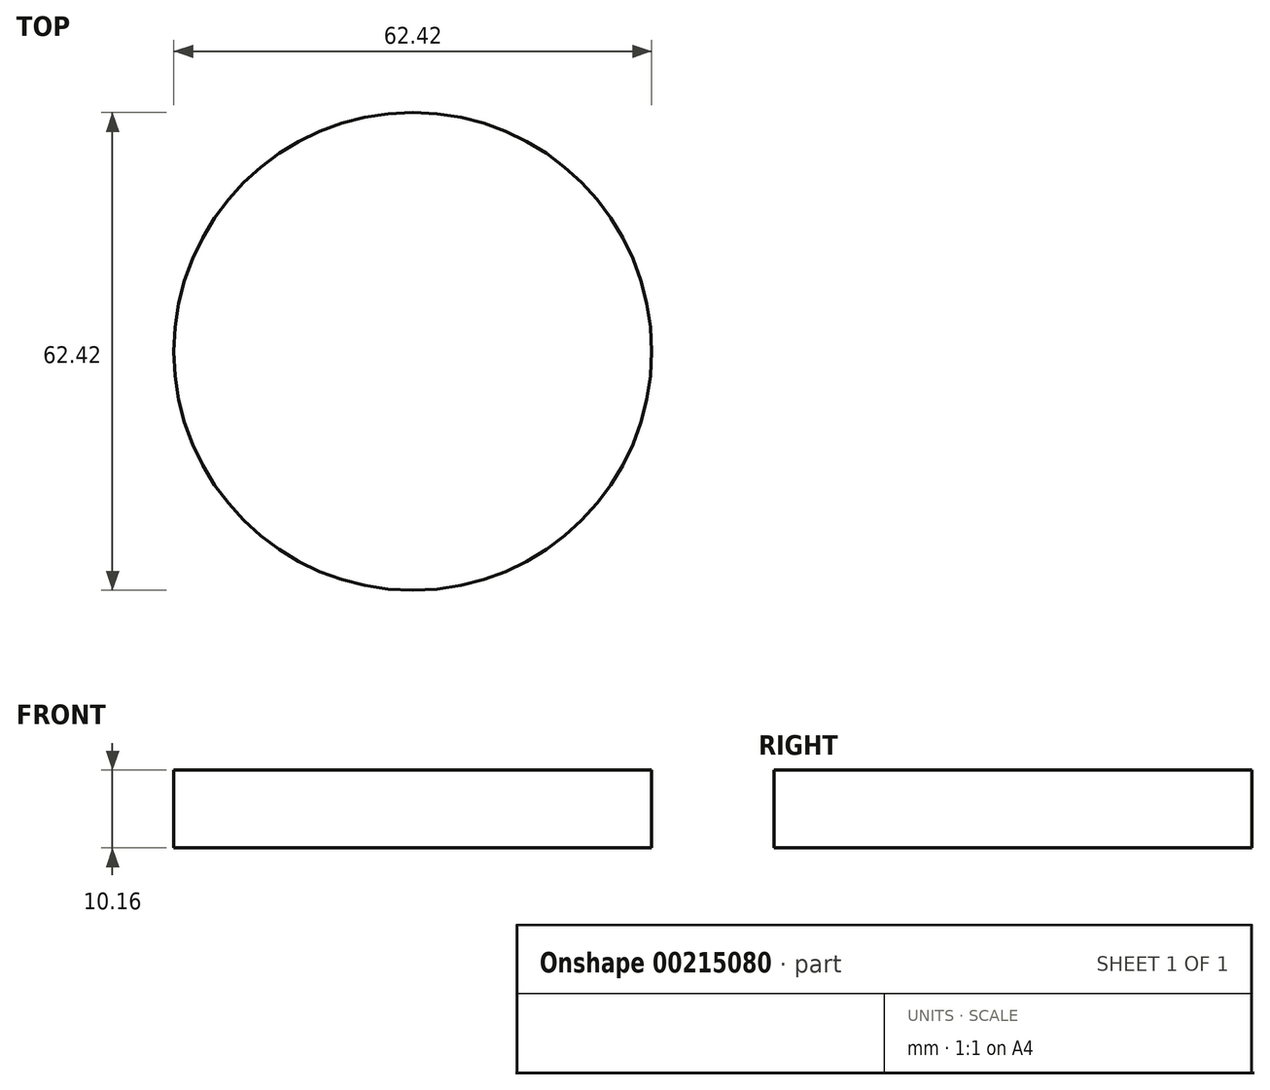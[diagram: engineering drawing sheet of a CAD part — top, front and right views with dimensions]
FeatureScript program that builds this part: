
annotation { "Feature Type Name" : "Feature", "Feature Type Description" : "" }
export const myFeature = defineFeature(function(context is Context, id is Id, definition is map)
    precondition{}
    {
        {
            var Q0;
            Q0=qCreatedBy(makeId("Top.planeOp"),FACE);
            var sketch = newSketch(context, id + "F0", { "sketchPlane" : qUnion([Q0])});
            skCircle(sketch, "E0", {"center": v(0, 0) * mm, "radius": 31.2 * mm});
            skSolve(sketch);
        }
        {
            var Q0;
            Q0=makeQuery(id+"F0.imprint","IMPRINT",FACE,{"disambiguationData":[TD([[makeQuery(id+"F0.imprint","IMPRINT",EDGE,{"derivedFrom":sQuery(id+"F0.wireOp",EDGE,"E0")}),1.0]])]});
            extrude(context, id + "F1", {"entities" : qUnion([Q0]), "depth" : 10.16 * mm});
        }
    });
